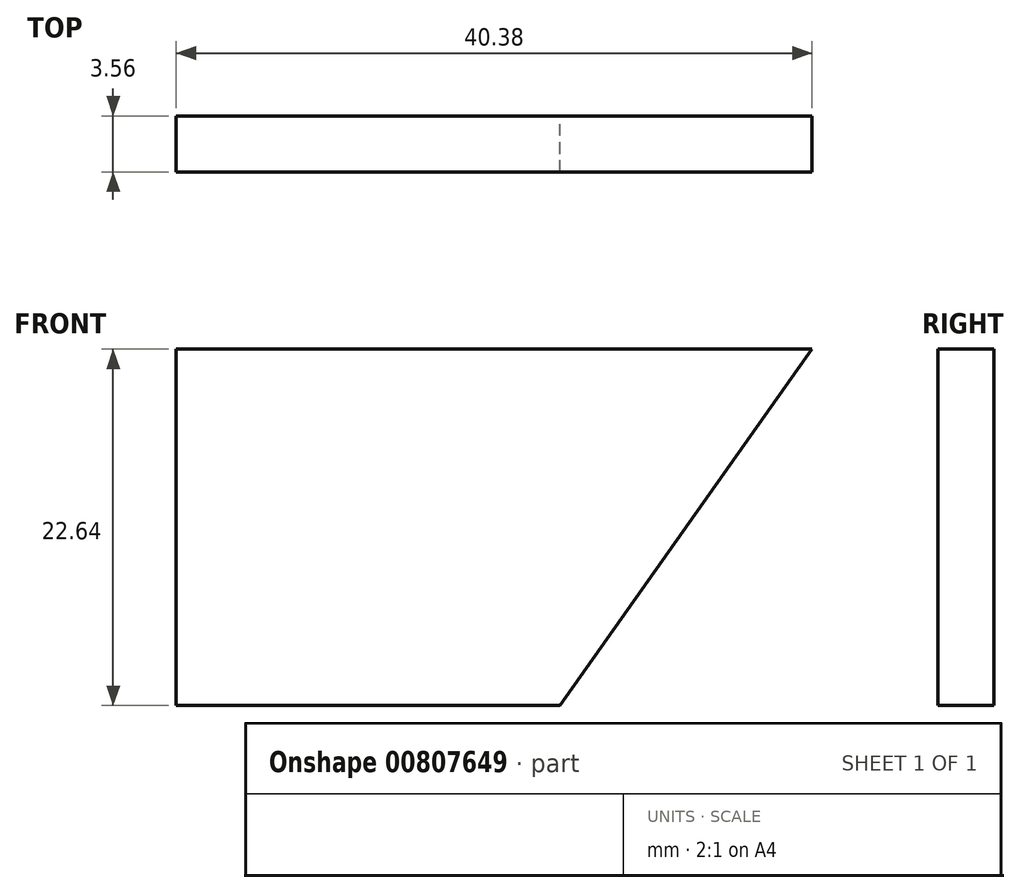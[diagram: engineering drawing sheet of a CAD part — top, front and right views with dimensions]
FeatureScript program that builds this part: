
annotation { "Feature Type Name" : "Feature", "Feature Type Description" : "" }
export const myFeature = defineFeature(function(context is Context, id is Id, definition is map)
    precondition{}
    {
        {
            var Q0;
            Q0=qCreatedBy(makeId("Front.planeOp"),FACE);
            var sketch = newSketch(context, id + "F0", { "sketchPlane" : qUnion([Q0])});
            skLineSegment(sketch, "E0.top", {"start": v(20.19, 11.32) * mm, "end": v(-20.19, 11.32) * mm});
            skLineSegment(sketch, "E0.right", {"start": v(-20.19, -11.32) * mm, "end": v(-20.19, 11.32) * mm});
            skPoint(sketch, "E0.middle", {"position": v(0, 0) * mm});
            skLineSegment(sketch, "E1", {"start": v(-20.19, -11.32) * mm, "end": v(4.17, -11.32) * mm});
            skLineSegment(sketch, "E2", {"start": v(4.17, -11.32) * mm, "end": v(20.19, 11.32) * mm});
            skSolve(sketch);
        }
        {
            var Q0;
            Q0 = qSketchRegion(id + "F0", true);
            extrude(context, id + "F1", {"entities" : qUnion([Q0]), "depth" : 3.56 * mm, "offsetDistance" : 25.4 * mm});
        }
    });
